# Revit family: Enave_100
name_source: partatom
category: Оборудование
units: mm (PartAtom-declared; Revit-internal decimal feet)

## family parameters
Всегда вертикально = Да
Классификация = Нет
На основе рабочей плоскости = Нет
Общий = Нет
При загрузке вырезать с полостями = Нет
Размер круглого соединителя = Использовать диаметр
Тип детали = Нормальный
Точка принадлежности помещению = Нет

## types (2) — shared parameters
00_20_Виробник = Вентс
00_20_Назва = Припливно-витяжна установка
D = 125 мм
H = 242 мм
L = 530 мм
URL = https://vents.ua
W = 520 мм
d = 115 мм
l = 420 мм
w = 410 мм
Вага = 8.00 кг
Висота = 242 мм
Довжина = 530 мм
Діаметр = 125 мм
Изготовитель = Вентс
Клас фільтрації = G4 / Coarse > 60%
Класифікація навантаження = HVAC
Кількість фаз = 1
Максимальний потік повітря = 130.0 м³/ч
Матеріал зони обслуговуваня = <По категории>
Матеріал корпусу = Поліпропілен (чорний)
Напруга = 230 В
Потужність = 38 Вт
Рівень звукового тиску на відстані 3 м = 32 дБА
Струм = 0 А
Ширина = 520 мм
zero-valued in all types: Отметка по умолчанию

## type names (no varying parameters)
- Enave-C 100 P А14
- Enave-CT 100 P А14

note: column(s) folded — value = type name in every type: 00_20_Тип
